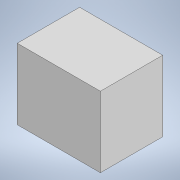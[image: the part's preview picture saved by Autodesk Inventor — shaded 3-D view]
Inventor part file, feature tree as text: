
AUTODESK INVENTOR PART (.ipt)
format: ipt  version: 2020 (Build 240168000, 168)  size: 84,480 bytes
history: native  units: mm
features: extrude x1, sketch x1
ambient origin geometry x8: Origin, YZ Plane, XZ Plane, XY Plane, X Axis, Y Axis, Z Axis, Center Point
bodies: Volumenkörper1 (feature_tree)
feature tree (2):
  extrude  "Extrusion1"  Depth=300.0mm
  sketch  "Skizze1"  dims[d0=400.0mm d1=300.0mm d2=340.0mm d3=0.0mm]
